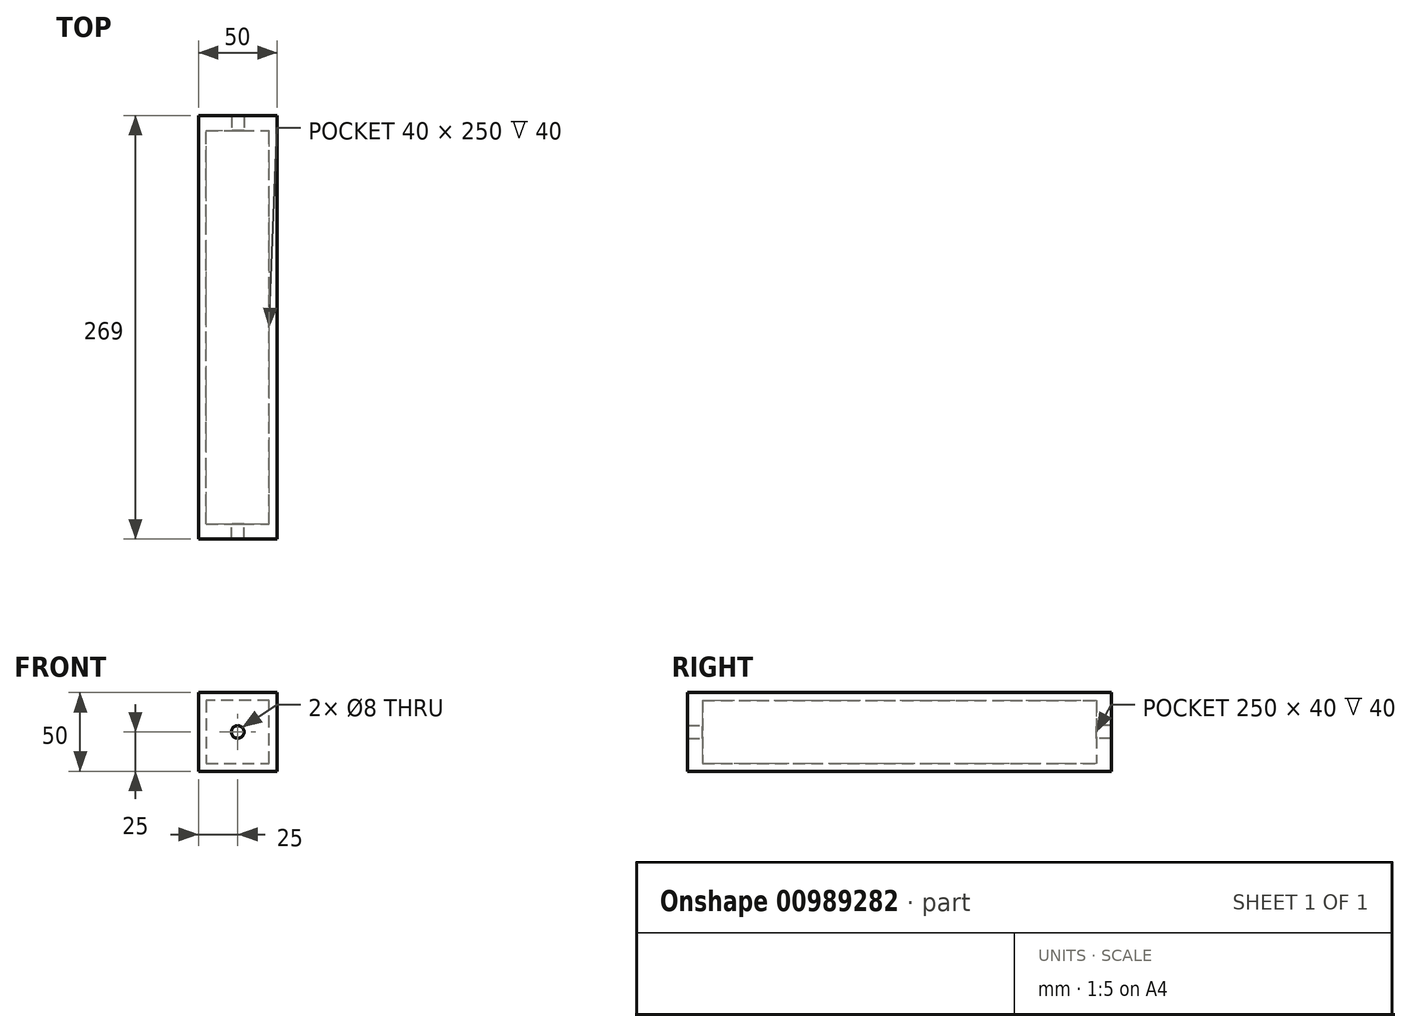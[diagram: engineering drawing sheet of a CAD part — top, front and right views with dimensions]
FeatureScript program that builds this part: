
annotation { "Feature Type Name" : "Feature", "Feature Type Description" : "" }
export const myFeature = defineFeature(function(context is Context, id is Id, definition is map)
    precondition{}
    {
        {
            var Q0;
            Q0=qCreatedBy(makeId("Front.planeOp"),FACE);
            var sketch = newSketch(context, id + "F0", { "sketchPlane" : qUnion([Q0])});
            skLineSegment(sketch, "E0", {"start": v(25, 0) * mm, "end": v(25, 25) * mm});
            skLineSegment(sketch, "E1", {"start": v(25, 25) * mm, "end": v(-25, 25) * mm});
            skLineSegment(sketch, "E2", {"start": v(-25, 25) * mm, "end": v(-25, -25) * mm});
            skLineSegment(sketch, "E3", {"start": v(-25, -25) * mm, "end": v(25, -25) * mm});
            skLineSegment(sketch, "E4", {"start": v(25, -25) * mm, "end": v(25, 0) * mm});
            skLineSegment(sketch, "E5", {"start": v(0, -20) * mm, "end": v(20, -20) * mm});
            skLineSegment(sketch, "E6", {"start": v(20, -20) * mm, "end": v(20, 20) * mm});
            skLineSegment(sketch, "E7", {"start": v(20, 20) * mm, "end": v(-20, 20) * mm});
            skLineSegment(sketch, "E8", {"start": v(-20, 20) * mm, "end": v(-20, -20) * mm});
            skLineSegment(sketch, "E9", {"start": v(-20, -20) * mm, "end": v(0, -20) * mm});
            skSolve(sketch);
        }
        {
            var Q0;
            Q0=makeQuery(id+"F0.imprint","IMPRINT",FACE,{"disambiguationData":[TD([[makeQuery(id+"F0.imprint","IMPRINT",EDGE,{"derivedFrom":sQuery(id+"F0.wireOp",EDGE,"E0")}),1.0]])]});
            extrude(context, id + "F1", {"entities" : qUnion([Q0]), "depth" : 250 * mm, "offsetDistance" : 25 * mm});
        }
        {
            var Q0;
            Q0=makeQuery(id+"F1.opExtrude","CAP_FACE",FACE,{"disambiguationData":[OSD([sQuery(id+"F0.wireOp",EDGE,"E0"),sQuery(id+"F0.wireOp",EDGE,"E1"),sQuery(id+"F0.wireOp",EDGE,"E2"),sQuery(id+"F0.wireOp",EDGE,"E3"),sQuery(id+"F0.wireOp",EDGE,"E4"),sQuery(id+"F0.wireOp",EDGE,"E5"),sQuery(id+"F0.wireOp",EDGE,"E6"),sQuery(id+"F0.wireOp",EDGE,"E7"),sQuery(id+"F0.wireOp",EDGE,"E8"),sQuery(id+"F0.wireOp",EDGE,"E9")])],"isStart":false});
            var sketch = newSketch(context, id + "F2", { "sketchPlane" : qUnion([Q0])});
            skLineSegment(sketch, "E10", {"start": v(-25, 25) * mm, "end": v(25, 25) * mm});
            skLineSegment(sketch, "E11", {"start": v(25, 25) * mm, "end": v(25, -25) * mm});
            skLineSegment(sketch, "E12", {"start": v(25, -25) * mm, "end": v(-25, -25) * mm});
            skLineSegment(sketch, "E13", {"start": v(-25, -25) * mm, "end": v(-25, 25) * mm});
            skCircle(sketch, "E14", {"center": v(0, 0) * mm, "radius": 4 * mm});
            skSolve(sketch);
        }
        {
            var Q0;
            Q0 = qSketchRegion(id + "F2", true);
            extrude(context, id + "F3", {"entities" : qUnion([Q0]), "operationType" : NewBodyOperationType.ADD, "depth" : 9.5 * mm, "offsetDistance" : 25 * mm});
        }
        {
            var Q0;
            Q0=makeQuery(id+"F0.imprint","IMPRINT",FACE,{"disambiguationData":[TD([[makeQuery(id+"F0.imprint","IMPRINT",EDGE,{"derivedFrom":sQuery(id+"F0.wireOp",EDGE,"E0")}),1.0]])]});
            var sketch = newSketch(context, id + "F4", { "sketchPlane" : qUnion([Q0])});
            skLineSegment(sketch, "E15", {"start": v(-25, 25) * mm, "end": v(25, 25) * mm});
            skLineSegment(sketch, "E16", {"start": v(25, 25) * mm, "end": v(25, -25) * mm});
            skLineSegment(sketch, "E17", {"start": v(25, -25) * mm, "end": v(-25, -25) * mm});
            skLineSegment(sketch, "E18", {"start": v(-25, -25) * mm, "end": v(-25, 25) * mm});
            skCircle(sketch, "E19", {"center": v(0, 0) * mm, "radius": 4 * mm});
            skSolve(sketch);
        }
        {
            var Q0;
            Q0 = qSketchRegion(id + "F4", true);
            extrude(context, id + "F5", {"entities" : qUnion([Q0]), "operationType" : NewBodyOperationType.ADD, "oppositeDirection" : true, "depth" : 9.5 * mm, "offsetDistance" : 25 * mm});
        }
    });
